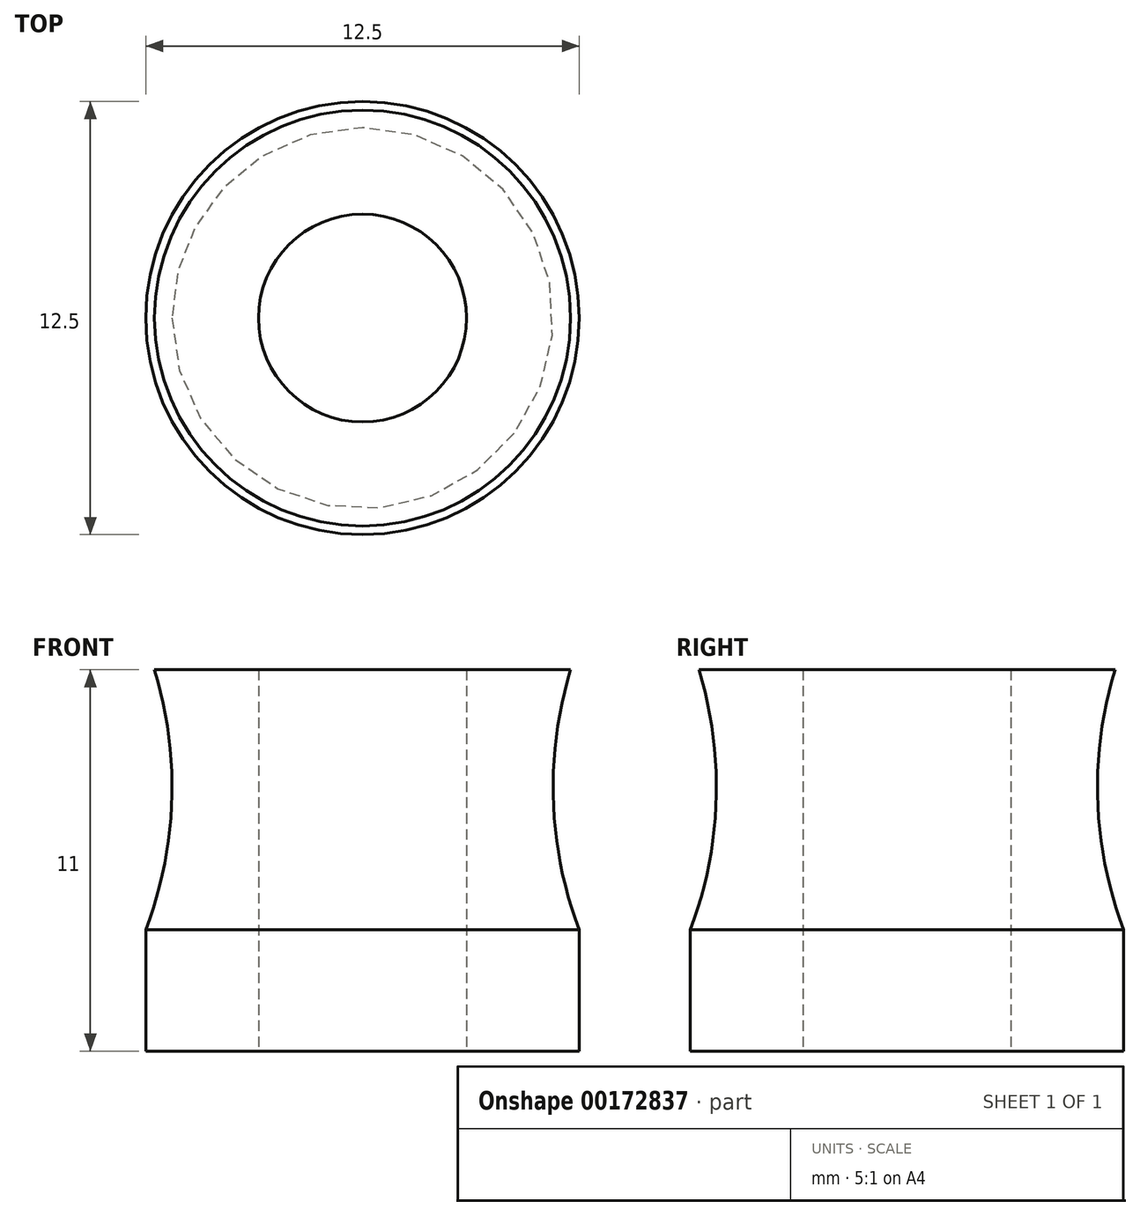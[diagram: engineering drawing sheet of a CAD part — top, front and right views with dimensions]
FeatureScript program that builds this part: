
annotation { "Feature Type Name" : "Feature", "Feature Type Description" : "" }
export const myFeature = defineFeature(function(context is Context, id is Id, definition is map)
    precondition{}
    {
        {
            var Q0;
            Q0=qCreatedBy(makeId("Front.planeOp"),FACE);
            var sketch = newSketch(context, id + "F0", { "sketchPlane" : qUnion([Q0])});
            skLineSegment(sketch, "E0", {"start": v(0, 0) * mm, "end": v(0, 11) * mm});
            skLineSegment(sketch, "E1", {"start": v(0, 11) * mm, "end": v(6, 11) * mm});
            skLineSegment(sketch, "E2", {"start": v(0, 0) * mm, "end": v(6.25, 0) * mm});
            skLineSegment(sketch, "E3", {"start": v(6.25, 0) * mm, "end": v(6.25, 3.5) * mm});
            skPoint(sketch, "E4", {"position": v(5.5, 7.25) * mm});
            skLineSegment(sketch, "E5", {"start": v(5.5, 7.25) * mm, "end": v(5.5, 11) * mm});
            skLineSegment(sketch, "E6", {"start": v(5.5, 7.25) * mm, "end": v(5.5, 3.5) * mm});
            skArc(sketch, "E7", {"start": v(6, 11) * mm, "mid": v(5.5, 7.23) * mm, "end": v(6.25, 3.5) * mm});
            skLineSegment(sketch, "E8", {"start": v(3, 11) * mm, "end": v(3, 0) * mm});
            skSolve(sketch);
        }
        {
            var Q0;
            {var subQ5=sQuery(id+"F0.wireOp",EDGE,"E3");Q0=makeQuery(id+"F0.imprint","IMPRINT",FACE,{"disambiguationData":[TD([[makeQuery(id+"F0.imprint","IMPRINT",EDGE,{"derivedFrom":subQ5}),1.0]])]});}
            var Q1;
            {var subQ0=sQuery(id+"F0.wireOp",EDGE,"E7");var subQ1=sQuery(id+"F0.wireOp",EDGE,"E1");var subQ2=makeQuery(id+"F0.imprint","INTERSECT",VERTEX,{"derivedFrom":[subQ1,subQ0]});Q1=makeQuery(id+"F0.imprint","IMPRINT",FACE,{"disambiguationData":[TD([[makeQuery(id+"F0.imprint","IMPRINT",EDGE,{"disambiguationData":[TD([[subQ2,1.0]])],"derivedFrom":subQ1}),-1.0]])]});}
            var Q2;
            Q2=sQuery(id+"F0.wireOp",EDGE,"E0");
            revolve(context, id + "F1", {"entities" : qUnion([Q0, Q1]), "axis" : qUnion([Q2]), "revolveType" : RevolveType.FULL});
        }
    });
